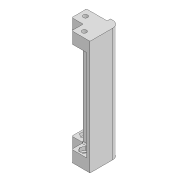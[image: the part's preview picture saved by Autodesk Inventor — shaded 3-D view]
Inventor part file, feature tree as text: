
AUTODESK INVENTOR PART (.ipt)
format: ipt  version: 2020 (Build 240168000, 168)  size: 241,152 bytes
history: native  units: mm
features: extrude x8, sketch x8, other x4, fillet x1
ambient origin geometry x8: Origin, YZ Plane, XZ Plane, XY Plane, X Axis, Y Axis, Z Axis, Center Point
bodies: Body1 (feature_tree)
feature tree (21):
  other  "Sólido1"
  extrude  "Extrusão1"  Depth=16.0mm
  extrude  "Extrusão2"  Depth=3.0mm
  extrude  "Extrusão3"  Depth=3.0mm
  extrude  "Extrusão4"  Depth=6.0mm
  extrude  "Extrusão5"  Depth=8.0mm
  fillet  "Arredondamento1"  Radius=100.0mm
  extrude  "Extrusão6"  Depth=10.0mm
  extrude  "Extrusão7"  TaperAngle=0.0deg  [1 undecoded]
  extrude  "Extrusão8"  Depth=5.0mm
  sketch  "Esboço1"  dims[d0=16.0mm d1=16.0mm]
  sketch  "Esboço2"  dims[d2=8.0mm d3=3.0mm]
  sketch  "Esboço3"  dims[d4=8.0mm d5=3.0mm]
  sketch  "Esboço4"  dims[d6=6.0mm d7=5.2mm]
  sketch  "Esboço5"  dims[d8=8.0mm d9=8.0mm d10=100.0mm d11=0.0mm]
  sketch  "Esboço6"  dims[d12=10.0mm d13=10.0mm]
  sketch  "Esboço7"  dims[d14=10.0mm d15=0.0mm d16=0.0mm]
  other  "Contorno projetado1"
  other  "Contorno projetado2"
  sketch  "Esboço9"  dims[d17=4.0mm d18=5.0mm d19=200.0mm d20=0.0mm d21=10.0mm d22=10.0mm d23=0.0mm d24=4.0mm d25=5.0mm d26=7.0mm d27=6.0mm d28=200.0mm d29=0.0mm d30=1.0mm d31=13.0mm d32=6.8mm d33=6.8mm d34=3.0mm d35=0.0mm d36=3.0mm d37=0.0mm d38=0.0mm d39=18.0mm d40=0.0mm]
  other  "Contorno projetado3"
note: 1 required parameter value undecoded (feature->parameter linkage not recoverable at this tier; creation-order binding heuristic only, values carry confidence <= 0.55)
